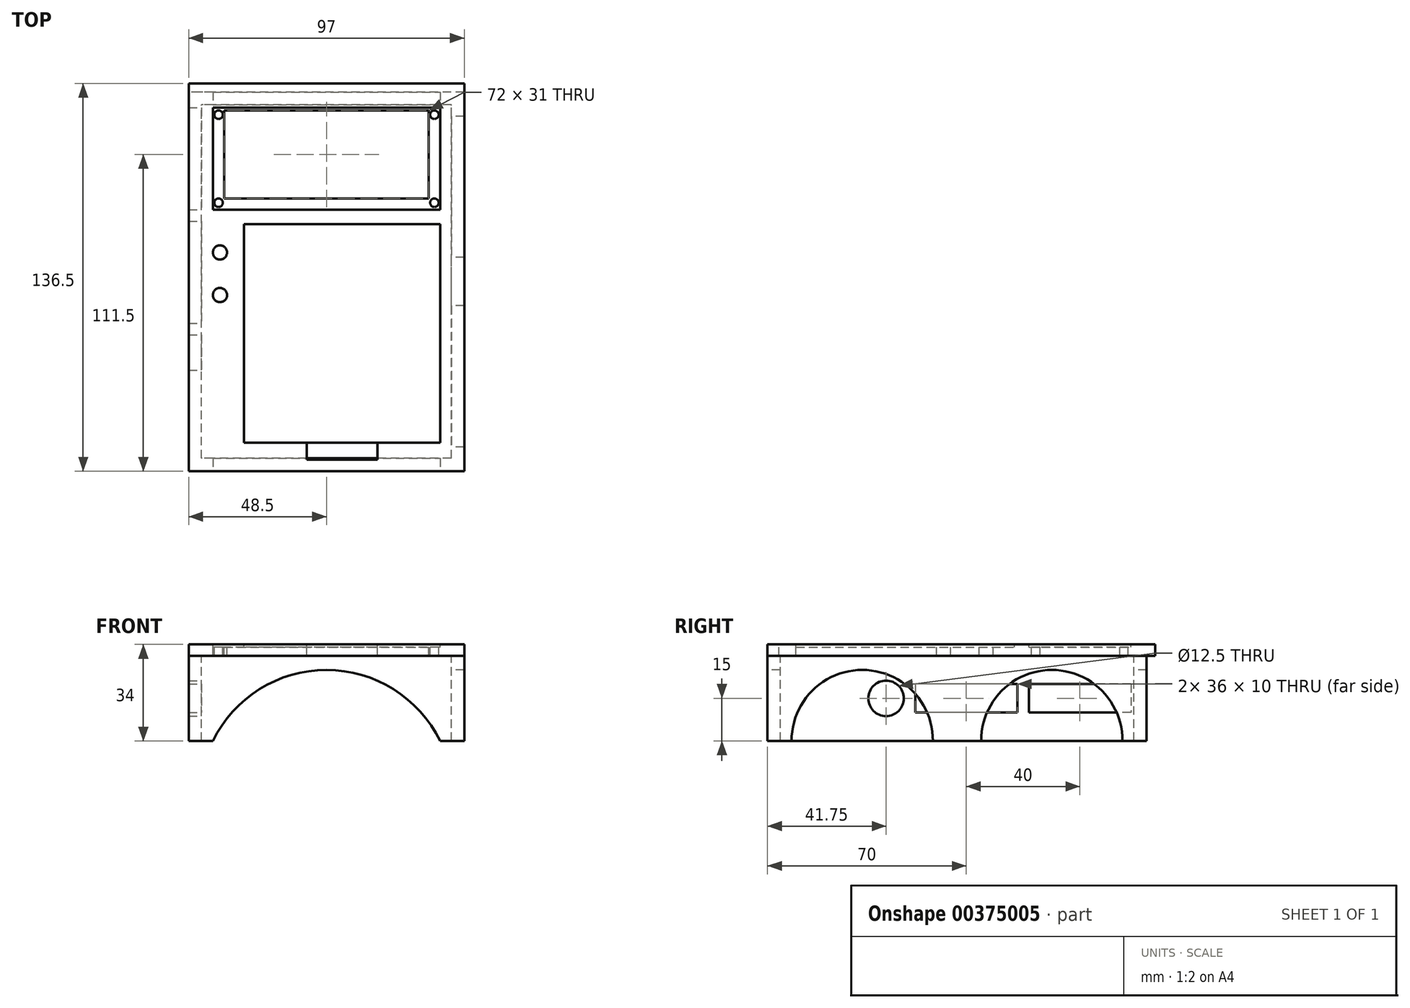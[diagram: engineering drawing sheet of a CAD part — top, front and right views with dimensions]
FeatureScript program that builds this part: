
annotation { "Feature Type Name" : "Feature", "Feature Type Description" : "" }
export const myFeature = defineFeature(function(context is Context, id is Id, definition is map)
    precondition{}
    {
        {
            var Q0;
            Q0=qCreatedBy(makeId("Top.planeOp"),FACE);
            var sketch = newSketch(context, id + "F0", { "sketchPlane" : qUnion([Q0])});
            skLineSegment(sketch, "E0.bottom", {"start": v(0, 0) * mm, "end": v(-69, 0) * mm});
            skLineSegment(sketch, "E0.top", {"start": v(0, 77) * mm, "end": v(-69, 77) * mm});
            skLineSegment(sketch, "E0.left", {"start": v(0, 0) * mm, "end": v(0, 77) * mm});
            skLineSegment(sketch, "E0.right", {"start": v(-69, 0) * mm, "end": v(-69, 77) * mm});
            skLineSegment(sketch, "E1.bottom", {"start": v(0, 82) * mm, "end": v(-80, 82) * mm});
            skLineSegment(sketch, "E1.top", {"start": v(0, 118) * mm, "end": v(-80, 118) * mm});
            skLineSegment(sketch, "E1.left", {"start": v(0, 82) * mm, "end": v(0, 118) * mm});
            skLineSegment(sketch, "E1.right", {"start": v(-80, 82) * mm, "end": v(-80, 118) * mm});
            skCircle(sketch, "E2", {"center": v(-77.5, 67) * mm, "radius": 2.5 * mm});
            skCircle(sketch, "E3", {"center": v(-77.5, 52) * mm, "radius": 2.5 * mm});
            skLineSegment(sketch, "E4.bottom", {"start": v(8.5, 126.5) * mm, "end": v(-88.5, 126.5) * mm});
            skLineSegment(sketch, "E4.top", {"start": v(8.5, -10) * mm, "end": v(-88.5, -10) * mm});
            skLineSegment(sketch, "E4.left", {"start": v(8.5, 126.5) * mm, "end": v(8.5, -10) * mm});
            skLineSegment(sketch, "E4.right", {"start": v(-88.5, 126.5) * mm, "end": v(-88.5, -10) * mm});
            skLineSegment(sketch, "E5.bottom", {"start": v(-76, 117) * mm, "end": v(-4, 117) * mm});
            skLineSegment(sketch, "E5.top", {"start": v(-76, 86) * mm, "end": v(-4, 86) * mm});
            skLineSegment(sketch, "E5.left", {"start": v(-76, 117) * mm, "end": v(-76, 86) * mm});
            skLineSegment(sketch, "E5.right", {"start": v(-4, 117) * mm, "end": v(-4, 86) * mm});
            skLineSegment(sketch, "E6.bottom", {"start": v(-47, 0) * mm, "end": v(-22, 0) * mm});
            skLineSegment(sketch, "E6.top", {"start": v(-47, -6) * mm, "end": v(-22, -6) * mm});
            skLineSegment(sketch, "E6.left", {"start": v(-47, 0) * mm, "end": v(-47, -6) * mm});
            skLineSegment(sketch, "E6.right", {"start": v(-22, 0) * mm, "end": v(-22, -6) * mm});
            skCircle(sketch, "E7", {"center": v(-78, 84.5) * mm, "radius": 1.5 * mm});
            skCircle(sketch, "E8.0.1.0", {"center": v(-78, 115.5) * mm, "radius": 1.5 * mm});
            skCircle(sketch, "E8.1.0.0", {"center": v(-2, 84.5) * mm, "radius": 1.5 * mm});
            skCircle(sketch, "E8.1.1.0", {"center": v(-2, 115.5) * mm, "radius": 1.5 * mm});
            skLineSegment(sketch, "E8.direction1", {"start": v(-78, 84.5) * mm, "end": v(-2, 84.5) * mm, "construction": true});
            skLineSegment(sketch, "E8.direction2", {"start": v(-78, 84.5) * mm, "end": v(-78, 115.5) * mm, "construction": true});
            skSolve(sketch);
        }
        {
            var Q0;
            Q0=makeQuery(id+"F0.imprint","IMPRINT",FACE,{"disambiguationData":[TD([[makeQuery(id+"F0.imprint","IMPRINT",EDGE,{"derivedFrom":sQuery(id+"F0.wireOp",EDGE,"E0.bottom")}),1.0]])]});
            var Q1;
            Q1=makeQuery(id+"F0.imprint","IMPRINT",FACE,{"disambiguationData":[TD([[makeQuery(id+"F0.imprint","IMPRINT",EDGE,{"derivedFrom":sQuery(id+"F0.wireOp",EDGE,"E0.top")}),-1.0]])]});
            extrude(context, id + "F1", {"entities" : qUnion([Q0, Q1]), "oppositeDirection" : true, "depth" : 4 * mm});
        }
        {
            var Q0;
            Q0=makeQuery(id+"F0.imprint","IMPRINT",FACE,{"disambiguationData":[TD([[makeQuery(id+"F0.imprint","IMPRINT",EDGE,{"derivedFrom":sQuery(id+"F0.wireOp",EDGE,"E0.bottom")}),-1.0]])]});
            var Q1;
            Q1=makeQuery(id+"F0.imprint","IMPRINT",FACE,{"disambiguationData":[TD([[makeQuery(id+"F0.imprint","IMPRINT",EDGE,{"derivedFrom":sQuery(id+"F0.wireOp",EDGE,"E1.bottom")}),-1.0]])]});
            extrude(context, id + "F2", {"entities" : qUnion([Q0, Q1]), "operationType" : NewBodyOperationType.ADD, "oppositeDirection" : true, "depth" : 4 * mm, "hasSecondDirection" : true, "secondDirectionOppositeDirection" : true, "secondDirectionDepth" : 1 * mm});
        }
        {
            var Q0;
            Q0=qCreatedBy(makeId("Top.planeOp"),FACE);
            var sketch = newSketch(context, id + "F3", { "sketchPlane" : qUnion([Q0])});
            skLineSegment(sketch, "E9.bottom", {"start": v(8.5, -10) * mm, "end": v(-88.5, -10) * mm});
            skLineSegment(sketch, "E9.top", {"start": v(8.5, 123.5) * mm, "end": v(-88.5, 123.5) * mm});
            skLineSegment(sketch, "E9.left", {"start": v(8.5, -10) * mm, "end": v(8.5, 123.5) * mm});
            skLineSegment(sketch, "E9.right", {"start": v(-88.5, -10) * mm, "end": v(-88.5, 123.5) * mm});
            skLineSegment(sketch, "E10.0", {"start": v(-84, -5.5) * mm, "end": v(-84, 119) * mm});
            skLineSegment(sketch, "E11.0", {"start": v(4, -5.5) * mm, "end": v(4, 119) * mm});
            skLineSegment(sketch, "E12.0", {"start": v(4, 119) * mm, "end": v(-84, 119) * mm});
            skLineSegment(sketch, "E13.0", {"start": v(4, -5.5) * mm, "end": v(-84, -5.5) * mm});
            skSolve(sketch);
        }
        {
            var Q0;
            Q0=makeQuery(id+"F3.imprint","IMPRINT",FACE,{"disambiguationData":[TD([[makeQuery(id+"F3.imprint","IMPRINT",EDGE,{"derivedFrom":sQuery(id+"F3.wireOp",EDGE,"E9.bottom")}),-1.0]])]});
            extrude(context, id + "F4", {"entities" : qUnion([Q0]), "oppositeDirection" : true, "depth" : 34 * mm, "hasSecondDirection" : true, "secondDirectionOppositeDirection" : true, "secondDirectionDepth" : 4 * mm});
        }
        {
            var Q0;
            Q0=qCreatedBy(makeId("Right.planeOp"),FACE);
            var sketch = newSketch(context, id + "F5", { "sketchPlane" : qUnion([Q0])});
            skLineSegment(sketch, "E14.bottom", {"start": v(118, -14) * mm, "end": v(82, -14) * mm});
            skLineSegment(sketch, "E14.top", {"start": v(118, -24) * mm, "end": v(82, -24) * mm});
            skLineSegment(sketch, "E14.left", {"start": v(118, -14) * mm, "end": v(118, -24) * mm});
            skLineSegment(sketch, "E14.right", {"start": v(82, -14) * mm, "end": v(82, -24) * mm});
            skLineSegment(sketch, "E15.1.0.0", {"start": v(78, -14) * mm, "end": v(42, -14) * mm});
            skLineSegment(sketch, "E15.1.0.1", {"start": v(78, -24) * mm, "end": v(42, -24) * mm});
            skLineSegment(sketch, "E15.1.0.2", {"start": v(78, -14) * mm, "end": v(78, -24) * mm});
            skLineSegment(sketch, "E15.1.0.3", {"start": v(42, -14) * mm, "end": v(42, -24) * mm});
            skLineSegment(sketch, "E15.direction1", {"start": v(82, -24) * mm, "end": v(42, -24) * mm, "construction": true});
            skPoint(sketch, "E16.centerSnap0", {"position": v(42, -19) * mm});
            skCircle(sketch, "E17", {"center": v(31.75, -19) * mm, "radius": 6.25 * mm});
            skSolve(sketch);
        }
        {
            var Q0;
            Q0=makeQuery(id+"F5.imprint","IMPRINT",FACE,{"disambiguationData":[TD([[makeQuery(id+"F5.imprint","IMPRINT",EDGE,{"derivedFrom":sQuery(id+"F5.wireOp",EDGE,"E15.1.0.0")}),1.0]])]});
            var Q1;
            Q1=makeQuery(id+"F5.imprint","IMPRINT",FACE,{"disambiguationData":[TD([[makeQuery(id+"F5.imprint","IMPRINT",EDGE,{"derivedFrom":sQuery(id+"F5.wireOp",EDGE,"E14.bottom")}),1.0]])]});
            var Q2;
            Q2=makeQuery(id+"F5.imprint","IMPRINT",FACE,{"disambiguationData":[TD([[makeQuery(id+"F5.imprint","IMPRINT",EDGE,{"derivedFrom":sQuery(id+"F5.wireOp",EDGE,"E17")}),1.0]])]});
            extrude(context, id + "F6", {"entities" : qUnion([Q0, Q1, Q2]), "operationType" : NewBodyOperationType.REMOVE, "oppositeDirection" : true, "depth" : 150 * mm});
        }
        {
            var Q0;
            Q0=qCreatedBy(makeId("Front.planeOp"),FACE);
            var sketch = newSketch(context, id + "F7", { "sketchPlane" : qUnion([Q0])});
            skArc(sketch, "E18", {"start": v(0, -34) * mm, "mid": v(-40, -9) * mm, "end": v(-80, -34) * mm});
            skPoint(sketch, "E18.first.point", {"position": v(-80, -34) * mm});
            skPoint(sketch, "E18.second.point", {"position": v(0, -34) * mm});
            skLineSegment(sketch, "E19", {"start": v(-80, -34) * mm, "end": v(0, -34) * mm});
            skSolve(sketch);
        }
        {
            var Q0;
            Q0=makeQuery(id+"F7.imprint","IMPRINT",FACE,{"disambiguationData":[TD([[makeQuery(id+"F7.imprint","IMPRINT",EDGE,{"derivedFrom":sQuery(id+"F7.wireOp",EDGE,"E18")}),1.0]])]});
            extrude(context, id + "F8", {"entities" : qUnion([Q0]), "operationType" : NewBodyOperationType.REMOVE, "oppositeDirection" : true, "depth" : 171.9 * mm, "hasSecondDirection" : true, "secondDirectionOppositeDirection" : false, "secondDirectionDepth" : 25 * mm});
        }
        {
            var Q0;
            Q0=qCreatedBy(makeId("Right.planeOp"),FACE);
            var sketch = newSketch(context, id + "F9", { "sketchPlane" : qUnion([Q0])});
            skPoint(sketch, "E20", {"position": v(115, -34) * mm});
            skPoint(sketch, "E21", {"position": v(65.25, -34) * mm});
            skArc(sketch, "E22", {"start": v(115, -34) * mm, "mid": v(90.12, -9) * mm, "end": v(65.25, -34) * mm});
            skLineSegment(sketch, "E23", {"start": v(115, -34) * mm, "end": v(65.25, -34) * mm});
            skLineSegment(sketch, "E24", {"start": v(56.75, 36.78) * mm, "end": v(56.75, -74.76) * mm, "construction": true});
            skLineSegment(sketch, "E25.MirrorCS", {"start": v(-1.5, -34) * mm, "end": v(48.25, -34) * mm});
            skArc(sketch, "E26.MirrorCS", {"start": v(-1.5, -34) * mm, "mid": v(23.37, -9) * mm, "end": v(48.25, -34) * mm});
            skSolve(sketch);
        }
        {
            var Q0;
            Q0=makeQuery(id+"F9.imprint","IMPRINT",FACE,{"disambiguationData":[TD([[makeQuery(id+"F9.imprint","IMPRINT",EDGE,{"derivedFrom":sQuery(id+"F9.wireOp",EDGE,"E25.MirrorCS")}),1.0]])]});
            var Q1;
            Q1=makeQuery(id+"F9.imprint","IMPRINT",FACE,{"disambiguationData":[TD([[makeQuery(id+"F9.imprint","IMPRINT",EDGE,{"derivedFrom":sQuery(id+"F9.wireOp",EDGE,"E22")}),1.0]])]});
            extrude(context, id + "F10", {"entities" : qUnion([Q0, Q1]), "operationType" : NewBodyOperationType.REMOVE, "depth" : 25 * mm});
        }
    });
